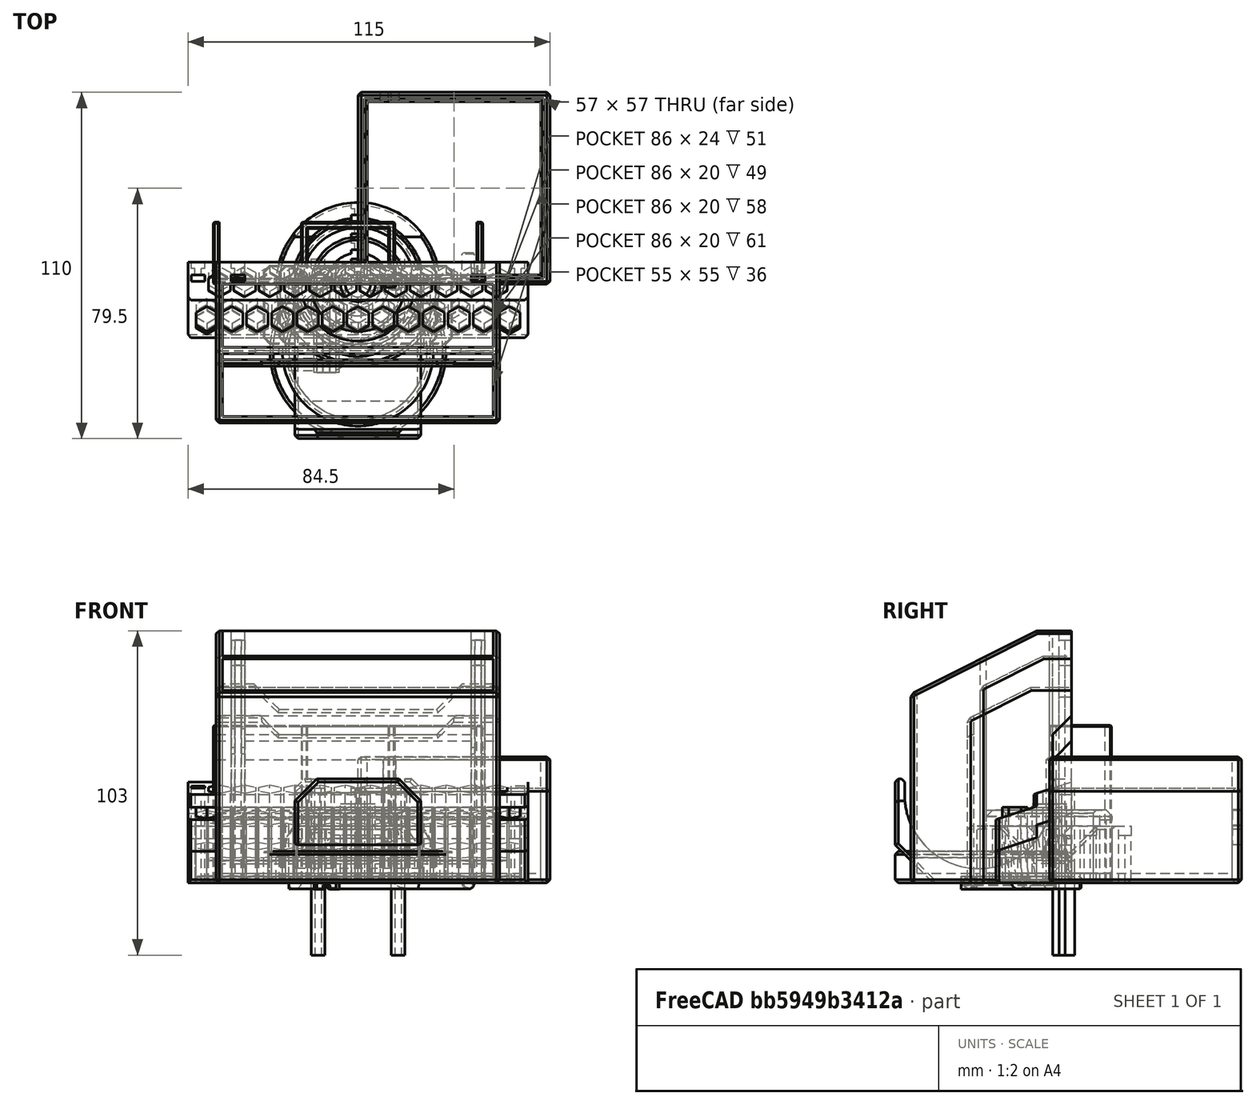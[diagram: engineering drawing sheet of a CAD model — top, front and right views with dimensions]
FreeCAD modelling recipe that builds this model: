
FCSTD DOCUMENT  (FreeCAD 0.18R14555 (Git shallow))
Label: peg-board-hook
License: All rights reserved
LicenseURL: http://en.wikipedia.org/wiki/All_rights_reserved
objects: Part::Feature×48, Part::Cut×36, Part::Chamfer×32, Part::Box×24, Part::Cylinder×17, Part::MultiFuse×11, Part::Torus×2, Part::MultiCommon×1, Part::Fillet×1
note: 172 computed .brp shape members not serialized (recipe doc carries the construction recipe); baked Part::Feature solids carry a one-line shape summary decoded from their .brp

FEATURE [Part::Torus] Torus
  Angle1 = -180
  Angle2 = 180
  Angle3 = 90
  AttacherType = Attacher::AttachEngine3D
  Placement = pos=(1e-15,5,0) rot=(0,0,1;3.14159rad)
  Radius1 = 5
  Radius2 = 2
FEATURE [Part::Cylinder] Cylinder
  Angle = 360
  AttacherType = Attacher::AttachEngine3D
  Height = 2
  Placement = pos=(0,0,0) rot=(0,1,0;1.5708rad)
  Radius = 2
FEATURE [Part::Cylinder] Cylinder001
  Angle = 360
  AttacherType = Attacher::AttachEngine3D
  Height = 9
  Placement = pos=(-7,-25.4,-2e-15) rot=(0,1,0;1.5708rad)
  Radius = 2
FEATURE [Part::Box] Box  label="Cube"
  AttacherType = Attacher::AttachEngine3D
  Height = 4
  Length = 1.9
  Placement = pos=(2,-28,-2) rot=(0,0,1;0rad)
  Width = 30
FEATURE [Part::Box] Box001  label="Cube001"
  AttacherType = Attacher::AttachEngine3D
  Height = 4
  Length = 1.9
  Placement = pos=(6.1,-28,-2) rot=(0,0,1;0rad)
  Width = 33
FEATURE [Part::Box] Box002  label="Cube002"
  AttacherType = Attacher::AttachEngine3D
  Height = 1.7
  Length = 6
  Placement = pos=(2,-28,-0.85) rot=(0,0,1;0rad)
  Width = 30
FEATURE [Part::MultiFuse] Fusion  label="mounter"
  Placement = pos=(-15,0,0) rot=(0,0,1;0rad)
  Shapes = -> [Box,Box002,Torus,Box001,Cylinder001,Cylinder]
FEATURE [Part::Box] Box003  label="Cube003"
  AttacherType = Attacher::AttachEngine3D
  Height = 33
  Length = 4.3
  Placement = pos=(-2.15,1,0) rot=(0,0,1;0rad)
  Width = 2
FEATURE [Part::Box] Box004  label="Cube004"
  AttacherType = Attacher::AttachEngine3D
  Height = 30
  Length = 4.3
  Placement = pos=(-2.15,5,0) rot=(0,0,1;0rad)
  Width = 3
FEATURE [Part::Box] Box005  label="Cube005"
  AttacherType = Attacher::AttachEngine3D
  Height = 30
  Length = 2
  Placement = pos=(-1,1,0) rot=(0,0,1;0rad)
  Width = 7
FEATURE [Part::Feature] Fusion001001  label="mounter-slot"
  Placement = pos=(-6,-28,-6e-15) rot=(0.57735,-0.57735,-0.57735;4.18879rad)
  shape: bbox 8 x 33 x 4.3 mm, 26 faces (baked)
FEATURE [Part::MultiFuse] Fusion001002  label="slot-template"
  Shapes = -> [Box004,Box005,Box003]
FEATURE [Part::Cylinder] Cylinder002
  Angle = 360
  AttacherType = Attacher::AttachEngine3D
  Height = 18
  Placement = pos=(0,-8,0) rot=(0,0,1;0rad)
  Radius = 10
FEATURE [Part::Cylinder] Cylinder003
  Angle = 360
  AttacherType = Attacher::AttachEngine3D
  Height = 18
  Placement = pos=(0,-8,0) rot=(0,0,1;0rad)
  Radius = 15
FEATURE [Part::Feature] Fusion001002001  label="Fusion001003"
  Placement = pos=(0,0,-15) rot=(0,0,1;0rad)
  shape: bbox 4.3 x 7 x 33 mm, 26 faces (baked)
FEATURE [Part::Cut] Cut
  Base = -> Cylinder003
  Tool = -> Cylinder002
FEATURE [Part::Feature] Fusion001002002  label="slot-template001"
  Placement = pos=(-50.8,0,-2) rot=(0,0,1;0rad)
  shape: bbox 4.3 x 7 x 33 mm, 14 faces (baked)
FEATURE [Part::Cut] Cut001  label="40mm-dia-ring"
  Base = -> Cut
  Tool = -> Fusion001002001
FEATURE [Part::Feature] Fusion001002003  label="slot-template002"
  Placement = pos=(50.8,0,-2) rot=(0,0,1;0rad)
  shape: bbox 4.3 x 7 x 33 mm, 14 faces (baked)
FEATURE [Part::Box] Box008  label="Cube008"
  AttacherType = Attacher::AttachEngine3D
  Height = 10
  Length = 113
  Placement = pos=(-57,-18,0) rot=(0,0,1;0rad)
  Width = 29
FEATURE [Part::Feature] Body014  label="Body001"
  Placement = pos=(-54,7,0) rot=(0,0,1;1.5708rad)
  shape: bbox 108 x 24 x 32 mm, 8 faces (baked)
FEATURE [Part::Cut] Cut002
  Base = -> Body014
  Tool = -> Fusion001002002
FEATURE [Part::Cut] Cut003
  Base = -> Cut002
  Tool = -> Fusion001002003
FEATURE [Part::Feature] Cut003001  label="Cut004"
  shape: bbox 108 x 24 x 32 mm, 30 faces (baked)
FEATURE [Part::Cut] Cut003002
  Base = -> Cut003
  Placement = pos=(0,0,-10) rot=(0,0,1;0rad)
  Tool = -> Box008
FEATURE [Part::Feature] Body015  label="bit-slot"
  shape: bbox 6.928 x 8 x 24 mm, 8 faces (baked)
FEATURE [Part::Feature] Body016  label="bit-slot001"
  Placement = pos=(-8,0,0) rot=(0,0,1;0rad)
  shape: bbox 6.928 x 8 x 24 mm, 8 faces (baked)
FEATURE [Part::Feature] Body017  label="bit-slot002"
  Placement = pos=(-16,0,0) rot=(0,0,1;0rad)
  shape: bbox 6.928 x 8 x 24 mm, 8 faces (baked)
FEATURE [Part::Feature] Body018  label="bit-slot003"
  Placement = pos=(-24,0,0) rot=(0,0,1;0rad)
  shape: bbox 6.928 x 8 x 24 mm, 8 faces (baked)
FEATURE [Part::Feature] Body019  label="bit-slot004"
  Placement = pos=(-32,0,0) rot=(0,0,1;0rad)
  shape: bbox 6.928 x 8 x 24 mm, 8 faces (baked)
FEATURE [Part::Feature] Body020  label="bit-slot005"
  Placement = pos=(-40,0,0) rot=(0,0,1;0rad)
  shape: bbox 6.928 x 8 x 24 mm, 8 faces (baked)
FEATURE [Part::Feature] Body021  label="bit-slot006"
  Placement = pos=(8,0,0) rot=(0,0,1;0rad)
  shape: bbox 6.928 x 8 x 24 mm, 8 faces (baked)
FEATURE [Part::Feature] Body022  label="bit-slot007"
  Placement = pos=(16,0,0) rot=(0,0,1;0rad)
  shape: bbox 6.928 x 8 x 24 mm, 8 faces (baked)
FEATURE [Part::Feature] Body023  label="bit-slot008"
  Placement = pos=(24,0,0) rot=(0,0,1;0rad)
  shape: bbox 6.928 x 8 x 24 mm, 8 faces (baked)
FEATURE [Part::Feature] Body024  label="bit-slot009"
  Placement = pos=(32,0,0) rot=(0,0,1;0rad)
  shape: bbox 6.928 x 8 x 24 mm, 8 faces (baked)
FEATURE [Part::Feature] Body025  label="bit-slot010"
  Placement = pos=(40,0,0) rot=(0,0,1;0rad)
  shape: bbox 6.928 x 8 x 24 mm, 8 faces (baked)
FEATURE [Part::Feature] Fusion001002004001  label="Fusion001002005"
  Placement = pos=(0,-11,0) rot=(0,0,1;0rad)
  shape: bbox 86.93 x 8 x 24 mm, 88 faces, 11 solids (baked)
FEATURE [Part::Feature] Body026  label="bit-slot011"
  Placement = pos=(48,-11,0) rot=(0,0,1;0rad)
  shape: bbox 6.928 x 8 x 24 mm, 8 faces (baked)
FEATURE [Part::Feature] Body027  label="bit-slot012"
  Placement = pos=(-48,-11,0) rot=(0,0,1;0rad)
  shape: bbox 6.928 x 8 x 24 mm, 8 faces (baked)
FEATURE [Part::MultiFuse] Fusion001002004002  label="bit-array-long"
  Shapes = -> [Fusion001002004001,Body027,Body026]
FEATURE [Part::Feature] Body028  label="bit-slot013"
  Placement = pos=(48,0,0) rot=(0,0,1;0rad)
  shape: bbox 6.928 x 8 x 24 mm, 8 faces (baked)
FEATURE [Part::MultiFuse] Fusion001002004003  label="bit-array-short"
  Placement = pos=(-4,0,0) rot=(0,0,1;0rad)
  Shapes = -> [Body028,Body022,Body015,Body020,Body025,Body019,Body017,Body018,Body021,Body016,Body023,Body024]
FEATURE [Part::Feature] Fusion001002004003001  label="bit-array-short001"
  Placement = pos=(-4,1.73889,7.4146) rot=(1,0,0;0.174533rad)
  shape: bbox 94.93 x 12.05 x 25.02 mm, 96 faces, 12 solids (baked)
FEATURE [Part::Feature] Fusion001002004002001  label="bit-array-long001"
  Placement = pos=(0,0.463863,3.12807) rot=(1,0,0;0.174533rad)
  shape: bbox 102.9 x 12.05 x 25.02 mm, 104 faces, 13 solids (baked)
FEATURE [Part::Cut] Cut003003
  Base = -> Cut003002
  Tool = -> Fusion001002004002001
FEATURE [Part::Cut] Cut003004
  Base = -> Cut003003
  Tool = -> Fusion001002004003001
FEATURE [Part::Feature] Fusion001002004002002  label="bit-array-long002"
  Placement = pos=(0,2.43348,3.47537) rot=(1,0,0;0.174533rad)
  shape: bbox 102.9 x 12.05 x 25.02 mm, 104 faces, 13 solids (baked)
FEATURE [Part::Feature] Fusion001002004003002  label="bit-array-short002"
  Placement = pos=(-4,0,7) rot=(0,0,1;0rad)
  shape: bbox 94.93 x 8 x 24 mm, 96 faces, 12 solids (baked)
FEATURE [Part::Cut] Cut003005
  Base = -> Cut003001
  Tool = -> Fusion001002004003002
FEATURE [Part::Cut] Cut003006
  Base = -> Cut003005
  Tool = -> Fusion001002004002002
FEATURE [Part::Chamfer] Chamfer  label="bit-holder-tall"
  Base = -> Cut003006
  Edges = 5 edges r=1: [Edge2,Edge3,Edge4,Edge115,Edge118]
FEATURE [Part::Chamfer] Chamfer001  label="bit-holder-short"
  Base = -> Cut003004
  Edges = 5 edges r=1: [Edge1,Edge2,Edge3,Edge6,Edge37]
FEATURE [Part::Feature] Cut001001  label="40mm-dia-ring001"
  Placement = pos=(0,8,0) rot=(0,0,1;0rad)
  shape: bbox 30 x 30 x 18 mm, 18 faces (baked)
FEATURE [Part::Box] Box009  label="Cube009"
  AttacherType = Attacher::AttachEngine3D
  Height = 12
  Length = 10
  Placement = pos=(-17,-5,6) rot=(0,0,1;0rad)
  Width = 10
FEATURE [Part::Cut] Cut003007
  Base = -> Cut001001
  Tool = -> Box009
FEATURE [Part::Chamfer] Chamfer002  label="40mm-dia-ring-caliper-holder"
  Base = -> Cut003007
  Edges = 2 edges r=2: [Edge14,Edge21]
FEATURE [Part::Feature] Fusion001002004003003  label="slot-template003"
  Placement = pos=(-38.1,0,29) rot=(0,0,1;0rad)
  shape: bbox 4.3 x 7 x 33 mm, 14 faces (baked)
FEATURE [Part::Box] Box010  label="Cube010"
  AttacherType = Attacher::AttachEngine3D
  Height = 60
  Length = 86
  Placement = pos=(-43,-24,2) rot=(0,0,1;0rad)
  Width = 24
FEATURE [Part::Feature] Fusion001002004003004  label="slot-template004"
  Placement = pos=(38.1,0,29) rot=(0,0,1;0rad)
  shape: bbox 4.3 x 7 x 33 mm, 14 faces (baked)
FEATURE [Part::Box] Box012  label="Cube012"
  AttacherType = Attacher::AttachEngine3D
  Height = 62
  Length = 90
  Placement = pos=(-45,-26,0) rot=(0,0,1;0rad)
  Width = 33
FEATURE [Part::Feature] Chamfer006001  label="cacualtor-holder-dual"
  shape: bbox 90 x 51 x 80 mm, 83 faces (baked)
FEATURE [Part::Box] Box015  label="Cube015"
  AttacherType = Attacher::AttachEngine3D
  Height = 12
  Length = 66
  Placement = pos=(-33,-27,54) rot=(0,0,1;0rad)
  Width = 13
FEATURE [Part::Chamfer] Chamfer006003
  Base = -> Box015
  Edges = 2 edges r=8: [Edge4,Edge8]
  Placement = pos=(0,0,-7) rot=(0,0,1;0rad)
FEATURE [Part::Feature] Chamfer006004001  label="caculator-holder-single001"
  shape: bbox 90 x 29 x 72 mm, 60 faces (baked)
FEATURE [Part::Chamfer] Chamfer006004002
  Base = -> Box012
  Edges = 1 edges: [Edge10 r1=10 r2=20]
FEATURE [Part::Cut] Cut003017
  Base = -> Chamfer006004002
  Tool = -> Box010
FEATURE [Part::Cut] Cut003018
  Base = -> Cut003017
  Tool = -> Chamfer006003
FEATURE [Part::Feature] Fusion001002004003005  label="slot-template005"
  Placement = pos=(38.1,0,-1) rot=(0,0,1;0rad)
  shape: bbox 4.3 x 7 x 33 mm, 14 faces (baked)
FEATURE [Part::MultiFuse] Fusion001002004003006
  Shapes = -> [Fusion001002004003005,Fusion001002004003004]
FEATURE [Part::Feature] Fusion001002004003007  label="slot-template006"
  Placement = pos=(-38.1,0,-1) rot=(0,0,1;0rad)
  shape: bbox 4.3 x 7 x 33 mm, 14 faces (baked)
FEATURE [Part::MultiFuse] Fusion001002004003008
  Shapes = -> [Fusion001002004003007,Fusion001002004003003]
FEATURE [Part::Cut] Cut003019
  Base = -> Cut003018
  Tool = -> Fusion001002004003006
FEATURE [Part::Cut] Cut003020
  Base = -> Cut003019
  Tool = -> Fusion001002004003008
FEATURE [Part::Chamfer] Chamfer006004003  label="multi-metter-holder"
  Base = -> Cut003020
  Edges = 14 edges r=1: [Edge1,Edge2,Edge3,Edge4,Edge6,Edge7,Edge8,Edge9,Edge10,Edge11,Edge12,Edge42,Edge45,Edge71]
FEATURE [Part::Cylinder] Cylinder004
  Angle = 360
  AttacherType = Attacher::AttachEngine3D
  Height = 22
  Placement = pos=(0,0,3) rot=(0,0,1;0rad)
  Radius = 5.5
FEATURE [Part::Cylinder] Cylinder005
  Angle = 360
  AttacherType = Attacher::AttachEngine3D
  Height = 16
  Placement = pos=(0,0,3) rot=(0,0,1;0rad)
  Radius = 20
FEATURE [Part::Cylinder] Cylinder006
  Angle = 360
  AttacherType = Attacher::AttachEngine3D
  Height = 18
  Radius = 26
FEATURE [Part::Feature] Fusion001002004003009  label="slot-template007"
  Placement = pos=(0,19,-15) rot=(0,0,1;0rad)
  shape: bbox 4.3 x 7 x 33 mm, 14 faces (baked)
FEATURE [Part::Box] Box016  label="Cube016"
  AttacherType = Attacher::AttachEngine3D
  Height = 10
  Length = 56
  Placement = pos=(-29,-15,9) rot=(0,0,1;0rad)
  Width = 30
FEATURE [Part::Chamfer] Chamfer006004004
  Base = -> Box016
  Edges = 2 edges r=9: [Edge9,Edge11]
FEATURE [Part::Cut] Cut003023
  Base = -> Cylinder006
  Tool = -> Cylinder005
FEATURE [Part::Cut] Cut003024
  Base = -> Cut003023
  Tool = -> Chamfer006004004
FEATURE [Part::Chamfer] Chamfer006004005
  Base = -> Cut003024
  Edges = 18 edges r=1: [Edge2,Edge3,Edge4,Edge5,Edge6,Edge7,Edge9,Edge10,Edge11,Edge13,Edge16,Edge17,Edge19,Edge21,Edge23,Edge25,Edge26,Edge28]
FEATURE [Part::Cut] Cut003025
  Base = -> Chamfer006004005
  Tool = -> Fusion001002004003009
FEATURE [Part::Cylinder] Cylinder007
  Angle = 360
  AttacherType = Attacher::AttachEngine3D
  Height = 27
  Radius = 4
FEATURE [Part::Cut] Cut003026
  Base = -> Cylinder004
  Tool = -> Cylinder007
FEATURE [Part::MultiFuse] Fusion001002004003010  label="bosch-head-holder"
  Shapes = -> [Cut003025,Cut003026]
FEATURE [Part::Feature] Fusion001002004003010001  label="bosch-head-holder001"
  shape: bbox 52 x 52 x 25 mm, 48 faces (baked)
FEATURE [Part::Feature] Fusion001002004003010002  label="slot-template008"
  Placement = pos=(0,13,-10) rot=(0,0,1;0rad)
  shape: bbox 4.3 x 7 x 33 mm, 14 faces (baked)
FEATURE [Part::Cylinder] Cylinder008
  Angle = 360
  AttacherType = Attacher::AttachEngine3D
  Height = 23
  Radius = 6.5
FEATURE [Part::Cylinder] Cylinder009
  Angle = 360
  AttacherType = Attacher::AttachEngine3D
  Height = 23
  Placement = pos=(0,0,3) rot=(0,0,1;0rad)
  Radius = 14
FEATURE [Part::Cylinder] Cylinder010
  Angle = 360
  AttacherType = Attacher::AttachEngine3D
  Height = 23
  Radius = 20
FEATURE [Part::Cut] Cut003027
  Base = -> Cylinder010
  Tool = -> Cylinder009
FEATURE [Part::Cut] Cut003028
  Base = -> Cut003027
  Tool = -> Cylinder008
FEATURE [Part::Chamfer] Chamfer006004006
  Base = -> Cut003028
  Edges = 3 edges r=1: [Edge3,Edge4,Edge8]
FEATURE [Part::Chamfer] Chamfer006004007
  Base = -> Chamfer006004006
  Edges = 1 edges r=2: [Edge3]
FEATURE [Part::Cut] Cut003029  label="hand-drill-mounter"
  Base = -> Chamfer006004007
  Tool = -> Fusion001002004003010002
FEATURE [Part::Feature] Fusion001002004003010003001  label="Fusion001002004003010004"
  shape: bbox 85.7 x 19.7 x 50 mm, 18 faces (baked)
FEATURE [Part::Chamfer] Chamfer006004008  label="cacualtor-holder-dual-seperator"
  Base = -> Fusion001002004003010003001
  Edges = 40 edges r=0.4: [Edge1,Edge3,Edge4,Edge5,Edge7,Edge8,Edge9,Edge10,Edge11,Edge12,Edge13,Edge14,Edge16,Edge17,Edge18,Edge19,Edge21,Edge23,Edge24,Edge25,Edge26,Edge27,Edge28,Edge29,Edge30,Edge31,Edge32,Edge33,Edge34,Edge35,Edge36,Edge40,Edge41,Edge42,Edge43,Edge44,Edge45,Edge46,Edge47,Edge48]
FEATURE [Part::Feature] Fusion001002004003010003002  label="slot-template009"
  Placement = pos=(-12.7,0,0) rot=(0,0,1;0rad)
  shape: bbox 4.3 x 7 x 33 mm, 26 faces (baked)
FEATURE [Part::Box] Box017  label="Cube017"
  AttacherType = Attacher::AttachEngine3D
  Height = 33
  Length = 40
  Placement = pos=(-20,-49,0) rot=(0,0,1;0rad)
  Width = 56
FEATURE [Part::Cylinder] Cylinder011
  Angle = 360
  AttacherType = Attacher::AttachEngine3D
  Height = 49
  Placement = pos=(25,-21.5,26) rot=(0,-1,0;1.5708rad)
  Radius = 23.5
  expr: Radius = 47 / 2
FEATURE [Part::Box] Box018  label="Cube018"
  AttacherType = Attacher::AttachEngine3D
  Height = 28
  Length = 52
  Placement = pos=(-27,-45,26.5) rot=(0,0,1;0rad)
  Width = 47
FEATURE [Part::MultiFuse] Fusion001002004003010003003
  Placement = pos=(0,-1,2) rot=(0,0,1;0rad)
  Shapes = -> [Cylinder011,Box018]
FEATURE [Part::Box] Box019  label="Cube019"
  AttacherType = Attacher::AttachEngine3D
  Height = 11
  Length = 11
  Placement = pos=(-21,-52,21) rot=(0,0,1;0rad)
  Width = 11
FEATURE [Part::Box] Box020  label="Cube020"
  AttacherType = Attacher::AttachEngine3D
  Height = 11
  Length = 11
  Placement = pos=(10,-52,21) rot=(0,0,1;0rad)
  Width = 11
FEATURE [Part::Chamfer] Chamfer006004010
  Base = -> Box019
  Edges = 1 edges r=7: [Edge8]
  Placement = pos=(-3,0,5) rot=(0,0,1;0rad)
FEATURE [Part::Chamfer] Chamfer006004011
  Base = -> Box020
  Edges = 1 edges r=7: [Edge4]
  Placement = pos=(3,0,5) rot=(0,0,1;0rad)
FEATURE [Part::Cut] Cut003030
  Base = -> Box017
  Tool = -> Fusion001002004003010003003
FEATURE [Part::Cut] Cut003031
  Base = -> Cut003030
  Tool = -> Chamfer006004011
FEATURE [Part::Cut] Cut003032
  Base = -> Cut003031
  Tool = -> Chamfer006004010
FEATURE [Part::Chamfer] Chamfer006004012
  Base = -> Cut003032
  Edges = 1 edges r=12: [Edge27]
FEATURE [Part::Chamfer] Chamfer006004013
  Base = -> Chamfer006004012
  Edges = 11 edges r=1: [Edge1,Edge2,Edge4,Edge11,Edge12,Edge14,Edge17,Edge18,Edge19,Edge20,Edge38]
FEATURE [Part::Chamfer] Chamfer006004014
  Base = -> Chamfer006004013
  Edges = 2 edges r=3: [Edge3,Edge16]
FEATURE [Part::Chamfer] Chamfer006004015
  Base = -> Chamfer006004014
  Edges = 3 edges r=1: [Edge15,Edge21,Edge23]
FEATURE [Part::Box] Box021  label="Cube021"
  AttacherType = Attacher::AttachEngine3D
  Height = 10
  Length = 3
  Placement = pos=(17,-2,-1) rot=(0,0,1;0rad)
  Width = 10
FEATURE [Part::Chamfer] Chamfer006004016
  Base = -> Box021
  Edges = 1 edges r=9: [Edge10]
  Placement = pos=(-13,0,0) rot=(0,0,1;0rad)
FEATURE [Part::Feature] Chamfer006004016001  label="Chamfer006004017"
  Placement = pos=(-24,0,0) rot=(0,0,1;0rad)
  shape: bbox 3 x 10 x 10 mm, 7 faces (baked)
FEATURE [Part::Feature] Fusion001002004003010003004  label="slot-template010"
  Placement = pos=(12.7,0,0) rot=(0,0,1;0rad)
  shape: bbox 4.3 x 7 x 33 mm, 26 faces (baked)
FEATURE [Part::Cut] Cut003033
  Base = -> Chamfer006004015
  Tool = -> Fusion001002004003010003002
FEATURE [Part::Cut] Cut003034
  Base = -> Cut003033
  Tool = -> Fusion001002004003010003004
FEATURE [Part::Cut] Cut003035
  Base = -> Cut003034
  Tool = -> Chamfer006004016
FEATURE [Part::Cut] Cut003036
  Base = -> Cut003035
  Tool = -> Chamfer006004016001
FEATURE [Part::Feature] Cut003040001  label="Cut003041"
  shape: bbox 61 x 62 x 40 mm, 23 faces (baked)
FEATURE [Part::Chamfer] Chamfer006004016003  label="ruler-holder-bottom"
  Base = -> Cut003040001
  Edges = 24 edges r=1: [Edge3,Edge8,Edge9,Edge10,Edge14,Edge16,Edge17,Edge21,Edge23,Edge24,Edge25,Edge26,Edge28,Edge33,Edge34,Edge35,Edge36,Edge40,Edge41,Edge47,Edge51,Edge54,Edge58,Edge62]
FEATURE [Part::Feature] Cut003040005001  label="Cut003040006"
  shape: bbox 61 x 62 x 30 mm, 22 faces (baked)
FEATURE [Part::Chamfer] Chamfer006004016005  label="ruler-holder-top"
  Base = -> Cut003040005001
  Edges = 28 edges r=1: [Edge2,Edge4,Edge5,Edge7,Edge11,Edge13,Edge19,Edge24,Edge25,Edge26,Edge30,Edge32,Edge33,Edge37,Edge39,Edge40,Edge41,Edge42,Edge44,Edge49,Edge50,Edge51,Edge52,Edge55,Edge56,Edge60,Edge61,Edge62]
FEATURE [Part::Feature] Fusion001002004003010003005  label="slot-template011"
  Placement = pos=(0,0,-18) rot=(0,0,1;0rad)
  shape: bbox 4.3 x 7 x 33 mm, 14 faces (baked)
FEATURE [Part::Cylinder] Cylinder012
  Angle = 360
  AttacherType = Attacher::AttachEngine3D
  Height = 10
  Placement = pos=(0,-21,5) rot=(0,0,1;0rad)
  Radius = 28
FEATURE [Part::Cylinder] Cylinder013
  Angle = 360
  AttacherType = Attacher::AttachEngine3D
  Height = 10
  Placement = pos=(0,-21,5) rot=(0,0,1;0rad)
  Radius = 22
FEATURE [Part::Cut] Cut003040005002
  Base = -> Cylinder012
  Placement = pos=(0,0,-5) rot=(0,0,1;0rad)
  Tool = -> Cylinder013
FEATURE [Part::Feature] Cut003040005002001  label="Cut003040005003"
  shape: bbox 56 x 56 x 10 mm, 4 faces (baked)
FEATURE [Part::Box] Box022  label="Cube022"
  AttacherType = Attacher::AttachEngine3D
  Height = 10
  Length = 26
  Placement = pos=(-13,-4,5) rot=(0,0,1;0rad)
  Width = 13
FEATURE [Part::Chamfer] Chamfer006004016006
  Base = -> Box022
  Edges = 2 edges r=5: [Edge2,Edge6]
FEATURE [Part::MultiCommon] Common
  Shapes = -> [Chamfer006004016006,Cut003040005002001]
FEATURE [Part::Chamfer] Chamfer006004016007
  Base = -> Cut003040005002
  Edges = 1 edges r=2: [Edge4]
FEATURE [Part::Chamfer] Chamfer006004016008
  Base = -> Chamfer006004016007
  Edges = 3 edges r=1: [Edge2,Edge6,Edge8]
FEATURE [Part::Chamfer] Chamfer006004016009
  Base = -> Common
  Edges = 2 edges r=2: [Edge4,Edge15]
FEATURE [Part::Chamfer] Chamfer006004016010
  Base = -> Chamfer006004016009
  Edges = 10 edges r=1: [Edge3,Edge5,Edge8,Edge10,Edge11,Edge13,Edge14,Edge18,Edge19,Edge20]
FEATURE [Part::MultiFuse] Fusion001002004003010003006
  Shapes = -> [Chamfer006004016010,Chamfer006004016008]
FEATURE [Part::Cut] Cut003040005002002  label="bosch-tail-holder"
  Base = -> Fusion001002004003010003006
  Tool = -> Fusion001002004003010003005
FEATURE [Part::Feature] Fusion001002004003010003007  label="slot-template012"
  Placement = pos=(-12.7,0,0) rot=(0,0,1;0rad)
  shape: bbox 4.3 x 7 x 33 mm, 14 faces (baked)
FEATURE [Part::Box] Box023  label="Cube023"
  AttacherType = Attacher::AttachEngine3D
  Height = 10
  Length = 50
  Placement = pos=(-25,-14,0) rot=(0,0,1;0rad)
  Width = 15
FEATURE [Part::Box] Box024  label="Cube024"
  AttacherType = Attacher::AttachEngine3D
  Height = 10
  Length = 60
  Placement = pos=(-30,-19,0) rot=(0,0,1;0rad)
  Width = 25
FEATURE [Part::Feature] Fusion001002004003010003008  label="slot-template013"
  Placement = pos=(12.7,0,0) rot=(0,0,1;0rad)
  shape: bbox 4.3 x 7 x 33 mm, 14 faces (baked)
FEATURE [Part::MultiFuse] Fusion001002004003010003009  label="dual-slot-template"
  Placement = pos=(0,0,-23) rot=(0,0,1;0rad)
  Shapes = -> [Fusion001002004003010003008,Fusion001002004003010003007]
FEATURE [Part::Feature] Fusion001002004003010003009001  label="dual-slot-template001"
  shape: bbox 29.7 x 7 x 33 mm, 28 faces, 2 solids (baked)
FEATURE [Part::Cut] Cut003040005002003
  Base = -> Box024
  Tool = -> Box023
FEATURE [Part::Chamfer] Chamfer006004016011
  Base = -> Cut003040005002003
  Edges = 8 edges r=2: [Edge1,Edge3,Edge6,Edge15,Edge21,Edge22,Edge23,Edge24]
FEATURE [Part::Chamfer] Chamfer006004016012
  Base = -> Chamfer006004016011
  Edges = 32 edges r=0.4: [Edge1,Edge4,Edge5,Edge6,Edge7,Edge8,Edge9,Edge10,Edge11,Edge12,Edge13,Edge14,Edge15,Edge16,Edge17,Edge18,Edge19,Edge20,Edge22,Edge24,Edge25,Edge26,Edge27,Edge28,Edge29,Edge30,Edge31,Edge32,Edge33,Edge34,Edge35,Edge36]
FEATURE [Part::Cut] Cut003040005002004  label="50-15-tool-slot"
  Base = -> Chamfer006004016012
  Tool = -> Fusion001002004003010003009001
FEATURE [Part::Box] Box025  label="Cube025"
  AttacherType = Attacher::AttachEngine3D
  Height = 10
  Length = 40
  Placement = pos=(-20,-12,0) rot=(0,0,1;0rad)
  Width = 15
FEATURE [Part::Box] Box026  label="Cube026"
  AttacherType = Attacher::AttachEngine3D
  Height = 10
  Length = 50
  Placement = pos=(-25,-17,0) rot=(0,0,1;0rad)
  Width = 25
FEATURE [Part::Feature] Fusion001002004003010003009002  label="dual-slot-template002"
  shape: bbox 29.7 x 7 x 33 mm, 28 faces, 2 solids (baked)
FEATURE [Part::Cut] Cut003040005002005
  Base = -> Box026
  Placement = pos=(0,-2,0) rot=(0,0,1;0rad)
  Tool = -> Box025
FEATURE [Part::Chamfer] Chamfer006004016013
  Base = -> Cut003040005002005
  Edges = 8 edges r=2: [Edge1,Edge3,Edge6,Edge15,Edge21,Edge22,Edge23,Edge24]
FEATURE [Part::Chamfer] Chamfer006004016014
  Base = -> Chamfer006004016013
  Edges = 32 edges r=0.4: [Edge1,Edge4,Edge5,Edge6,Edge7,Edge8,Edge9,Edge10,Edge11,Edge12,Edge13,Edge14,Edge15,Edge16,Edge17,Edge18,Edge19,Edge20,Edge22,Edge24,Edge25,Edge26,Edge27,Edge28,Edge29,Edge30,Edge31,Edge32,Edge33,Edge34,Edge35,Edge36]
FEATURE [Part::Cut] Cut003040005002006  label="40-15-tool-slot"
  Base = -> Chamfer006004016014
  Tool = -> Fusion001002004003010003009002
FEATURE [Part::Feature] Fusion001002004003010003009003  label="mounter001"
  shape: bbox 15.58 x 33 x 4 mm, 22 faces (baked)
FEATURE [Part::Cylinder] Cylinder014
  Angle = 360
  AttacherType = Attacher::AttachEngine3D
  Height = 32
  Placement = pos=(-7,-10,-1.6e-15) rot=(0,1,0;1.5708rad)
  Radius = 2
FEATURE [Part::Torus] Torus001
  Angle1 = -180
  Angle2 = 180
  Angle3 = 90
  AttacherType = Attacher::AttachEngine3D
  Placement = pos=(25,8e-15,0) rot=(0,0,1;4.71239rad)
  Radius1 = 10
  Radius2 = 2
FEATURE [Part::Box] Box027  label="Cube027"
  AttacherType = Attacher::AttachEngine3D
  Height = 10
  Length = 10
  Placement = pos=(-14,2,-4) rot=(0,0,1;0rad)
  Width = 10
FEATURE [Part::Cut] Cut003040005002007
  Base = -> Fusion001002004003010003009003
  Tool = -> Box027
FEATURE [Part::Fillet] Fillet
  Base = -> Cut003040005002007
  Edges = 4 edges r=1: [Edge4,Edge23,Edge53,Edge55]
FEATURE [Part::Cylinder] Cylinder015
  Angle = 360
  AttacherType = Attacher::AttachEngine3D
  Height = 32
  Placement = pos=(-9.19239,-26.163,7.5e-15) rot=(0.774597,-0.447214,0.447214;4.45971rad)
  Radius = 2
FEATURE [Part::Box] Box028  label="Cube028"
  AttacherType = Attacher::AttachEngine3D
  Height = 10
  Length = 10
  Placement = pos=(-11,-8,-4) rot=(0,0,1;0rad)
  Width = 10
FEATURE [Part::Chamfer] Chamfer006004016016
  Base = -> Box028
  Edges = 1 edges r=4: [Edge1]
FEATURE [Part::Cut] Cut003040005002008
  Base = -> Fillet
  Tool = -> Chamfer006004016016
FEATURE [Part::Chamfer] Chamfer006004016017
  Base = -> Cut003040005002008
  Edges = 2 edges r=0.4: [Edge64,Edge69]
FEATURE [Part::Cylinder] Cylinder016
  Angle = 360
  AttacherType = Attacher::AttachEngine3D
  Height = 10
  Placement = pos=(35,0,0) rot=(1,0,0;4.71239rad)
  Radius = 2
FEATURE [Part::Chamfer] Chamfer006004016018
  Base = -> Cylinder016
  Edges = 1 edges r=0.4: [Edge1]
FEATURE [Part::MultiFuse] Fusion001002004003010003009004
  Shapes = -> [Cylinder014,Chamfer006004016018,Cylinder015,Torus001,Chamfer006004016017]
